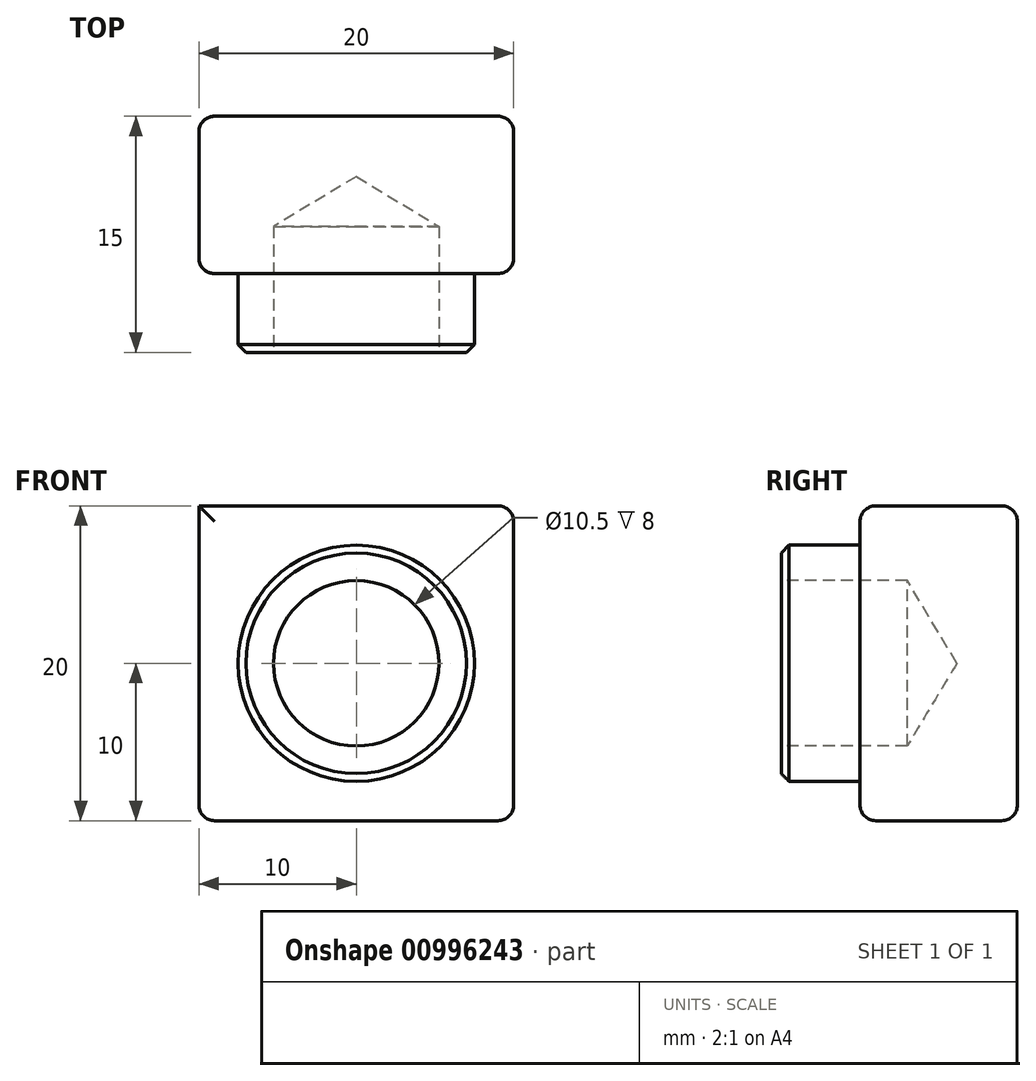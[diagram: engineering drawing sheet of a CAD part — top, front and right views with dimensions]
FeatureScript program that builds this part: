
annotation { "Feature Type Name" : "Feature", "Feature Type Description" : "" }
export const myFeature = defineFeature(function(context is Context, id is Id, definition is map)
    precondition{}
    {
        {
            var Q0;
            Q0=qCreatedBy(makeId("Front.planeOp"),FACE);
            var sketch = newSketch(context, id + "F0", { "sketchPlane" : qUnion([Q0])});
            skLineSegment(sketch, "E0.bottom", {"start": v(-10, 10) * mm, "end": v(10, 10) * mm});
            skLineSegment(sketch, "E0.top", {"start": v(-10, -10) * mm, "end": v(10, -10) * mm});
            skLineSegment(sketch, "E0.left", {"start": v(-10, 10) * mm, "end": v(-10, -10) * mm});
            skLineSegment(sketch, "E0.right", {"start": v(10, 10) * mm, "end": v(10, -10) * mm});
            skSolve(sketch);
        }
        {
            var Q0;
            Q0=makeQuery(id+"F0.imprint","IMPRINT",FACE,{"disambiguationData":[TD([[makeQuery(id+"F0.imprint","IMPRINT",EDGE,{"derivedFrom":sQuery(id+"F0.wireOp",EDGE,"E0.bottom")}),-1.0]])]});
            extrude(context, id + "F1", {"entities" : qUnion([Q0]), "depth" : 10 * mm, "offsetDistance" : 25 * mm});
        }
        {
            var Q0;
            Q0=makeQuery(id+"F1.opExtrude","CAP_FACE",FACE,{"disambiguationData":[OSD([sQuery(id+"F0.wireOp",EDGE,"E0.bottom"),sQuery(id+"F0.wireOp",EDGE,"E0.top"),sQuery(id+"F0.wireOp",EDGE,"E0.left"),sQuery(id+"F0.wireOp",EDGE,"E0.right")])],"isStart":false});
            var sketch = newSketch(context, id + "F2", { "sketchPlane" : qUnion([Q0])});
            skCircle(sketch, "E1", {"center": v(0, 0) * mm, "radius": 7.5 * mm});
            skSolve(sketch);
        }
        {
            var Q0;
            Q0 = qSketchRegion(id + "F2", true);
            extrude(context, id + "F3", {"entities" : qUnion([Q0]), "operationType" : NewBodyOperationType.ADD, "depth" : 5 * mm, "offsetDistance" : 25 * mm});
        }
        {
            var Q0;
            Q0=makeQuery(id+"F3.opExtrude","CAP_FACE",FACE,{"disambiguationData":[OSD([sQuery(id+"F2.wireOp",EDGE,"E1")])],"isStart":false});
            var sketch = newSketch(context, id + "F4", { "sketchPlane" : qUnion([Q0])});
            skPoint(sketch, "E2", {"position": v(0, 0) * mm});
            skSolve(sketch);
        }
        {
            var Q0;
            Q0=sQuery(id+"F4.wireOp",VERTEX,"E2");
            var Q1;
            Q1=makeQuery(id+"F1.opExtrude","SWEPT_BODY",BODY,{"disambiguationData":[OSD([sQuery(id+"F0.wireOp",EDGE,"E0.bottom"),sQuery(id+"F0.wireOp",EDGE,"E0.top"),sQuery(id+"F0.wireOp",EDGE,"E0.left"),sQuery(id+"F0.wireOp",EDGE,"E0.right")])]});
            hole(context, id + "F5", {"style" : HoleStyle.SIMPLE, "endStyle" : HoleEndStyle.BLIND, "standardTappedOrClearance" : lookupTablePath({ "standard" : "ISO", "engagement" : "75%", "pitch" : "1.5 mm", "size" : "M12", "type" : "Tapped" }), "standardBlindInLast" : lookupTablePath({ "standard" : "ISO", "fit" : "Normal", "engagement" : "75%", "pitch" : "1.5 mm", "size" : "M12", "type" : "Clearance & tapped" }), "holeDiameter" : 10.5 * mm, "majorDiameter" : 12 * mm, "showTappedDepth" : true, "holeDepth" : 8 * mm, "isTappedThrough" : true, "tappedDepth" : 3.5 * mm, "tapClearance" : 3, "locations" : qUnion([Q0]), "scope" : qUnion([Q1])});
        }
        {
            var Q0;
            Q0=makeQuery(id+"F1.opExtrude","CAP_EDGE",EDGE,{"disambiguationData":[OSD([sQuery(id+"F0.wireOp",EDGE,"E0.bottom")])],"isStart":false});
            var Q1;
            Q1=makeQuery(id+"F1.opExtrude","CAP_EDGE",EDGE,{"disambiguationData":[OSD([sQuery(id+"F0.wireOp",EDGE,"E0.left")])],"isStart":false});
            var Q2;
            Q2=makeQuery(id+"F1.opExtrude","CAP_EDGE",EDGE,{"disambiguationData":[OSD([sQuery(id+"F0.wireOp",EDGE,"E0.top")])],"isStart":false});
            var Q3;
            Q3=makeQuery(id+"F1.opExtrude","CAP_EDGE",EDGE,{"disambiguationData":[OSD([sQuery(id+"F0.wireOp",EDGE,"E0.right")])],"isStart":false});
            var Q4;
            Q4=makeQuery(id+"F1.opExtrude","SWEPT_EDGE",EDGE,{"disambiguationData":[OSD([sQuery(id+"F0.wireOp",EDGE,"E0.top"),sQuery(id+"F0.wireOp",EDGE,"E0.left")])]});
            var Q5;
            Q5=makeQuery(id+"F1.opExtrude","CAP_EDGE",EDGE,{"disambiguationData":[OSD([sQuery(id+"F0.wireOp",EDGE,"E0.top")])],"isStart":true});
            var Q6;
            Q6=makeQuery(id+"F1.opExtrude","SWEPT_EDGE",EDGE,{"disambiguationData":[OSD([sQuery(id+"F0.wireOp",EDGE,"E0.top"),sQuery(id+"F0.wireOp",EDGE,"E0.right")])]});
            var Q7;
            Q7=makeQuery(id+"F1.opExtrude","SWEPT_EDGE",EDGE,{"disambiguationData":[OSD([sQuery(id+"F0.wireOp",EDGE,"E0.bottom"),sQuery(id+"F0.wireOp",EDGE,"E0.right")])]});
            var Q8;
            Q8=makeQuery(id+"F1.opExtrude","CAP_EDGE",EDGE,{"disambiguationData":[OSD([sQuery(id+"F0.wireOp",EDGE,"E0.right")])],"isStart":true});
            var Q9;
            Q9=makeQuery(id+"F1.opExtrude","CAP_EDGE",EDGE,{"disambiguationData":[OSD([sQuery(id+"F0.wireOp",EDGE,"E0.left")])],"isStart":true});
            var Q10;
            Q10=makeQuery(id+"F1.opExtrude","CAP_EDGE",EDGE,{"disambiguationData":[OSD([sQuery(id+"F0.wireOp",EDGE,"E0.bottom")])],"isStart":true});
            fillet(context, id + "F6", {"entities" : qUnion([Q0, Q1, Q2, Q3, Q4, Q5, Q6, Q7, Q8, Q9, Q10]), "radius" : 1 * mm, "tangentPropagation" : true, "allowEdgeOverflow" : false});
        }
        {
            var Q0;
            Q0=makeQuery(id+"F3.opExtrude","CAP_EDGE",EDGE,{"disambiguationData":[OSD([sQuery(id+"F2.wireOp",EDGE,"E1")])],"isStart":false});
            chamfer(context, id + "F7", {"entities" : qUnion([Q0]), "width" : 0.5 * mm, "tangentPropagation" : true});
        }
    });
